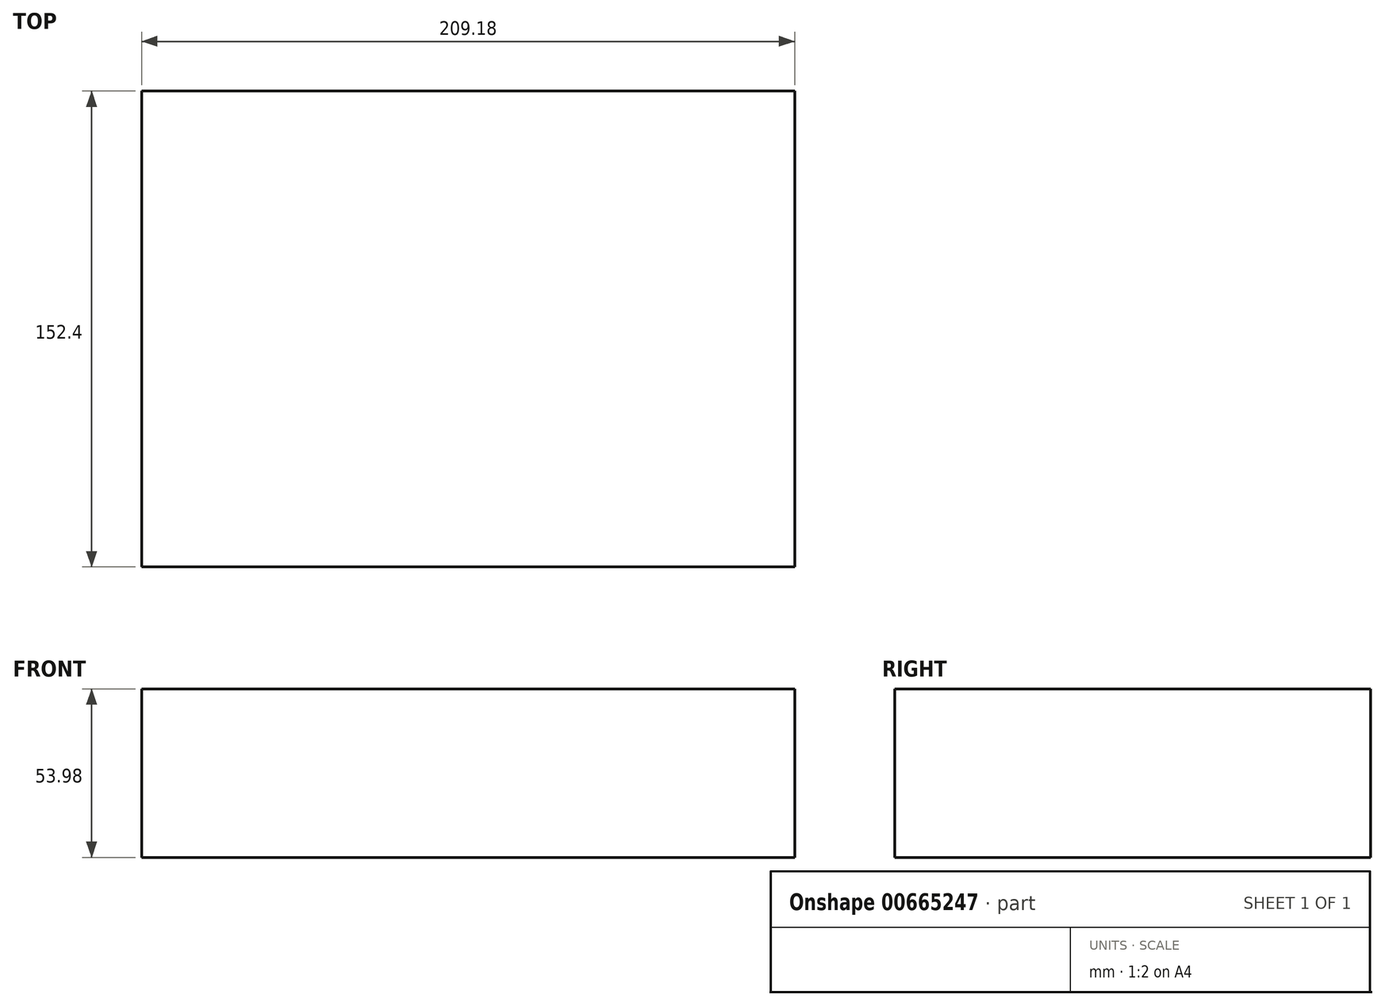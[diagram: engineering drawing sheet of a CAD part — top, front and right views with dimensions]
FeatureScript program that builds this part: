
annotation { "Feature Type Name" : "Feature", "Feature Type Description" : "" }
export const myFeature = defineFeature(function(context is Context, id is Id, definition is map)
    precondition{}
    {
        {
            var Q0;
            Q0=qCreatedBy(makeId("Front.planeOp"),FACE);
            var sketch = newSketch(context, id + "F0", { "sketchPlane" : qUnion([Q0])});
            skLineSegment(sketch, "E0.bottom", {"start": v(-113.48, 25.31) * mm, "end": v(95.7, 25.31) * mm});
            skLineSegment(sketch, "E0.top", {"start": v(-113.48, -28.67) * mm, "end": v(95.7, -28.67) * mm});
            skLineSegment(sketch, "E0.left", {"start": v(-113.48, 25.31) * mm, "end": v(-113.48, -28.67) * mm});
            skLineSegment(sketch, "E0.right", {"start": v(95.7, 25.31) * mm, "end": v(95.7, -28.67) * mm});
            skSolve(sketch);
        }
        {
            var Q0;
            Q0 = qSketchRegion(id + "F0", true);
            extrude(context, id + "F1", {"entities" : qUnion([Q0]), "depth" : 152.4 * mm, "offsetDistance" : 25.4 * mm});
        }
    });
